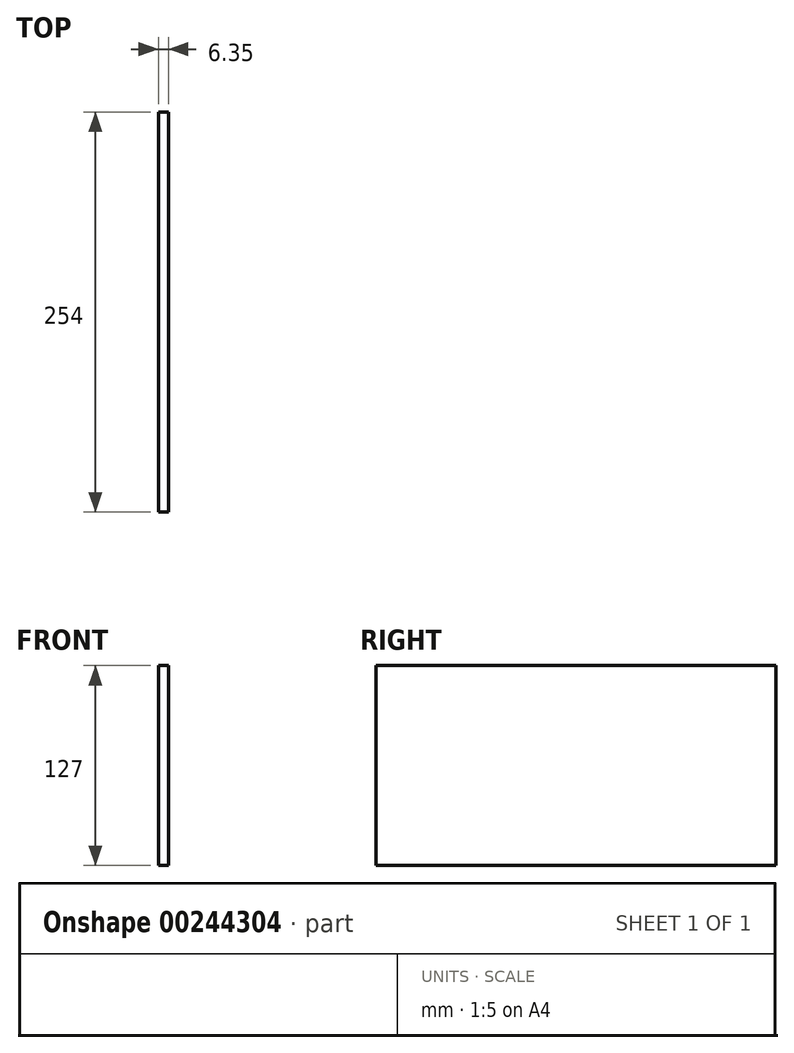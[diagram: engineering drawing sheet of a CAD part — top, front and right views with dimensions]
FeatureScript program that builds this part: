
annotation { "Feature Type Name" : "Feature", "Feature Type Description" : "" }
export const myFeature = defineFeature(function(context is Context, id is Id, definition is map)
    precondition{}
    {
        {
            var Q0;
            Q0=qCreatedBy(makeId("Right.planeOp"),FACE);
            var sketch = newSketch(context, id + "F0", { "sketchPlane" : qUnion([Q0])});
            skLineSegment(sketch, "E0.bottom", {"start": v(167.4, 68.97) * mm, "end": v(-86.6, 68.97) * mm});
            skLineSegment(sketch, "E0.top", {"start": v(167.4, -58.03) * mm, "end": v(-86.6, -58.03) * mm});
            skLineSegment(sketch, "E0.left", {"start": v(167.4, 68.97) * mm, "end": v(167.4, -58.03) * mm});
            skLineSegment(sketch, "E0.right", {"start": v(-86.6, 68.97) * mm, "end": v(-86.6, -58.03) * mm});
            skSolve(sketch);
        }
        {
            var Q0;
            Q0 = qSketchRegion(id + "F0", true);
            extrude(context, id + "F1", {"entities" : qUnion([Q0]), "depth" : 6.35 * mm});
        }
    });
